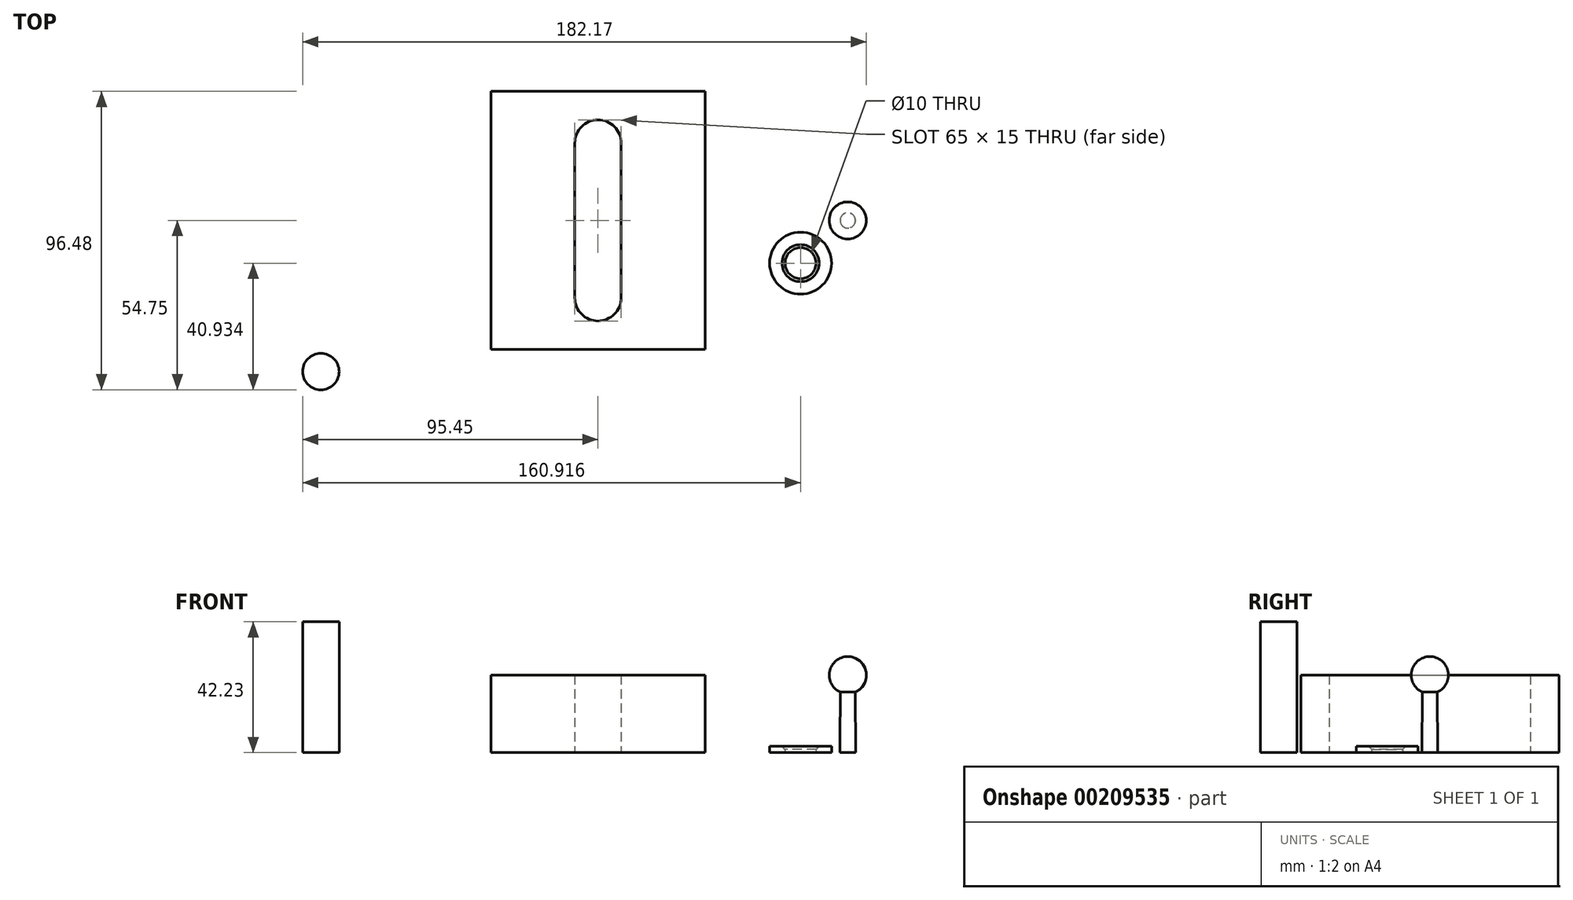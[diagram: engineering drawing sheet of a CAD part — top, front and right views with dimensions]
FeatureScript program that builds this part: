
annotation { "Feature Type Name" : "Feature", "Feature Type Description" : "" }
export const myFeature = defineFeature(function(context is Context, id is Id, definition is map)
    precondition{}
    {
        {
            var Q0;
            Q0=qCreatedBy(makeId("Top.planeOp"),FACE);
            var sketch = newSketch(context, id + "F0", { "sketchPlane" : qUnion([Q0])});
            skCircle(sketch, "E0", {"center": v(0, 25) * mm, "radius": 7.5 * mm});
            skLineSegment(sketch, "E1", {"start": v(-31.68, 0) * mm, "end": v(29.64, 0) * mm});
            skLineSegment(sketch, "E2", {"start": v(-7.5, 25) * mm, "end": v(-7.5, 0) * mm});
            skLineSegment(sketch, "E3", {"start": v(7.5, 25) * mm, "end": v(7.5, 0) * mm});
            skLineSegment(sketch, "E4.0.MirrorCS", {"start": v(7.5, -25) * mm, "end": v(7.5, 0) * mm});
            skCircle(sketch, "E4.1.MirrorC", {"center": v(0, -25) * mm, "radius": 7.5 * mm});
            skLineSegment(sketch, "E4.2.MirrorCS", {"start": v(-7.5, -25) * mm, "end": v(-7.5, 0) * mm});
            skLineSegment(sketch, "E5.rect.bottom", {"start": v(34.61, -41.73) * mm, "end": v(-34.61, -41.73) * mm});
            skLineSegment(sketch, "E5.rect.top", {"start": v(34.61, 41.73) * mm, "end": v(-34.61, 41.73) * mm});
            skLineSegment(sketch, "E5.rect.left", {"start": v(34.61, -41.73) * mm, "end": v(34.61, 41.73) * mm});
            skLineSegment(sketch, "E5.rect.right", {"start": v(-34.61, -41.73) * mm, "end": v(-34.61, 41.73) * mm});
            skPoint(sketch, "E5.rect.middle", {"position": v(0, 0) * mm});
            skSolve(sketch);
        }
        {
            var Q0;
            {var subQ4=sQuery(id+"F0.wireOp",EDGE,"E2");Q0=makeQuery(id+"F0.imprint","IMPRINT",FACE,{"disambiguationData":[TD([[makeQuery(id+"F0.imprint","IMPRINT",EDGE,{"derivedFrom":subQ4}),-1.0]])]});}
            extrude(context, id + "F1", {"entities" : qUnion([Q0]), "depth" : 25 * mm});
        }
        {
            var Q0;
            Q0=qCreatedBy(makeId("Top.planeOp"),FACE);
            var sketch = newSketch(context, id + "F2", { "sketchPlane" : qUnion([Q0])});
            skCircle(sketch, "E6", {"center": v(-89.56, -48.86) * mm, "radius": 5.9 * mm});
            skSolve(sketch);
        }
        {
            var Q0;
            Q0=makeQuery(id+"F2.imprint","IMPRINT",FACE,{"disambiguationData":[TD([[makeQuery(id+"F2.imprint","IMPRINT",EDGE,{"derivedFrom":sQuery(id+"F2.wireOp",EDGE,"E6")}),1.0]])]});
            extrude(context, id + "F3", {"entities" : qUnion([Q0]), "depth" : 42.23 * mm});
        }
        {
            var Q0;
            Q0=qCreatedBy(makeId("Front.planeOp"),FACE);
            var sketch = newSketch(context, id + "F4", { "sketchPlane" : qUnion([Q0])});
            skLineSegment(sketch, "E7", {"start": v(80.72, 0) * mm, "end": v(80.72, 31) * mm});
            skCircle(sketch, "E8", {"center": v(80.72, 25) * mm, "radius": 6 * mm});
            skLineSegment(sketch, "E9.bottom", {"start": v(80.72, 0) * mm, "end": v(83.22, 0) * mm});
            skLineSegment(sketch, "E9.top", {"start": v(80.72, 25) * mm, "end": v(83.16, 25) * mm});
            skLineSegment(sketch, "E9.right", {"start": v(83.22, 0) * mm, "end": v(83.16, 25) * mm});
            skSolve(sketch);
        }
        {
            var Q0;
            {var subQ3=sQuery(id+"F4.wireOp",EDGE,"E9.top");Q0=makeQuery(id+"F4.imprint","IMPRINT",FACE,{"disambiguationData":[TD([[makeQuery(id+"F4.imprint","IMPRINT",EDGE,{"derivedFrom":subQ3}),1.0]])]});}
            var Q1;
            {var subQ3=sQuery(id+"F4.wireOp",EDGE,"E9.top");Q1=makeQuery(id+"F4.imprint","IMPRINT",FACE,{"disambiguationData":[TD([[makeQuery(id+"F4.imprint","IMPRINT",EDGE,{"derivedFrom":subQ3}),-1.0]])]});}
            var Q2;
            {var subQ3=sQuery(id+"F4.wireOp",EDGE,"E9.bottom");Q2=makeQuery(id+"F4.imprint","IMPRINT",FACE,{"disambiguationData":[TD([[makeQuery(id+"F4.imprint","IMPRINT",EDGE,{"derivedFrom":subQ3}),1.0]])]});}
            var Q3;
            Q3=sQuery(id+"F4.wireOp",EDGE,"E7");
            revolve(context, id + "F5", {"entities" : qUnion([Q0, Q1, Q2]), "axis" : qUnion([Q3]), "revolveType" : RevolveType.FULL});
        }
        {
            var Q0;
            Q0=qCreatedBy(makeId("Top.planeOp"),FACE);
            var sketch = newSketch(context, id + "F6", { "sketchPlane" : qUnion([Q0])});
            skCircle(sketch, "E10", {"center": v(65.47, -13.82) * mm, "radius": 10 * mm});
            skCircle(sketch, "E11", {"center": v(65.47, -13.82) * mm, "radius": 5 * mm});
            skSolve(sketch);
        }
        {
            var Q0;
            Q0=makeQuery(id+"F6.imprint","IMPRINT",FACE,{"disambiguationData":[TD([[makeQuery(id+"F6.imprint","IMPRINT",EDGE,{"derivedFrom":sQuery(id+"F6.wireOp",EDGE,"E10")}),1.0]])]});
            extrude(context, id + "F7", {"entities" : qUnion([Q0]), "depth" : 2 * mm});
        }
        {
            var Q0;
            Q0=makeQuery(id+"F7.opExtrude","CAP_EDGE",EDGE,{"disambiguationData":[OSD([sQuery(id+"F6.wireOp",EDGE,"E11")])],"isStart":false});
            chamfer(context, id + "F8", {"entities" : qUnion([Q0]), "width" : 1 * mm, "tangentPropagation" : true});
        }
    });
